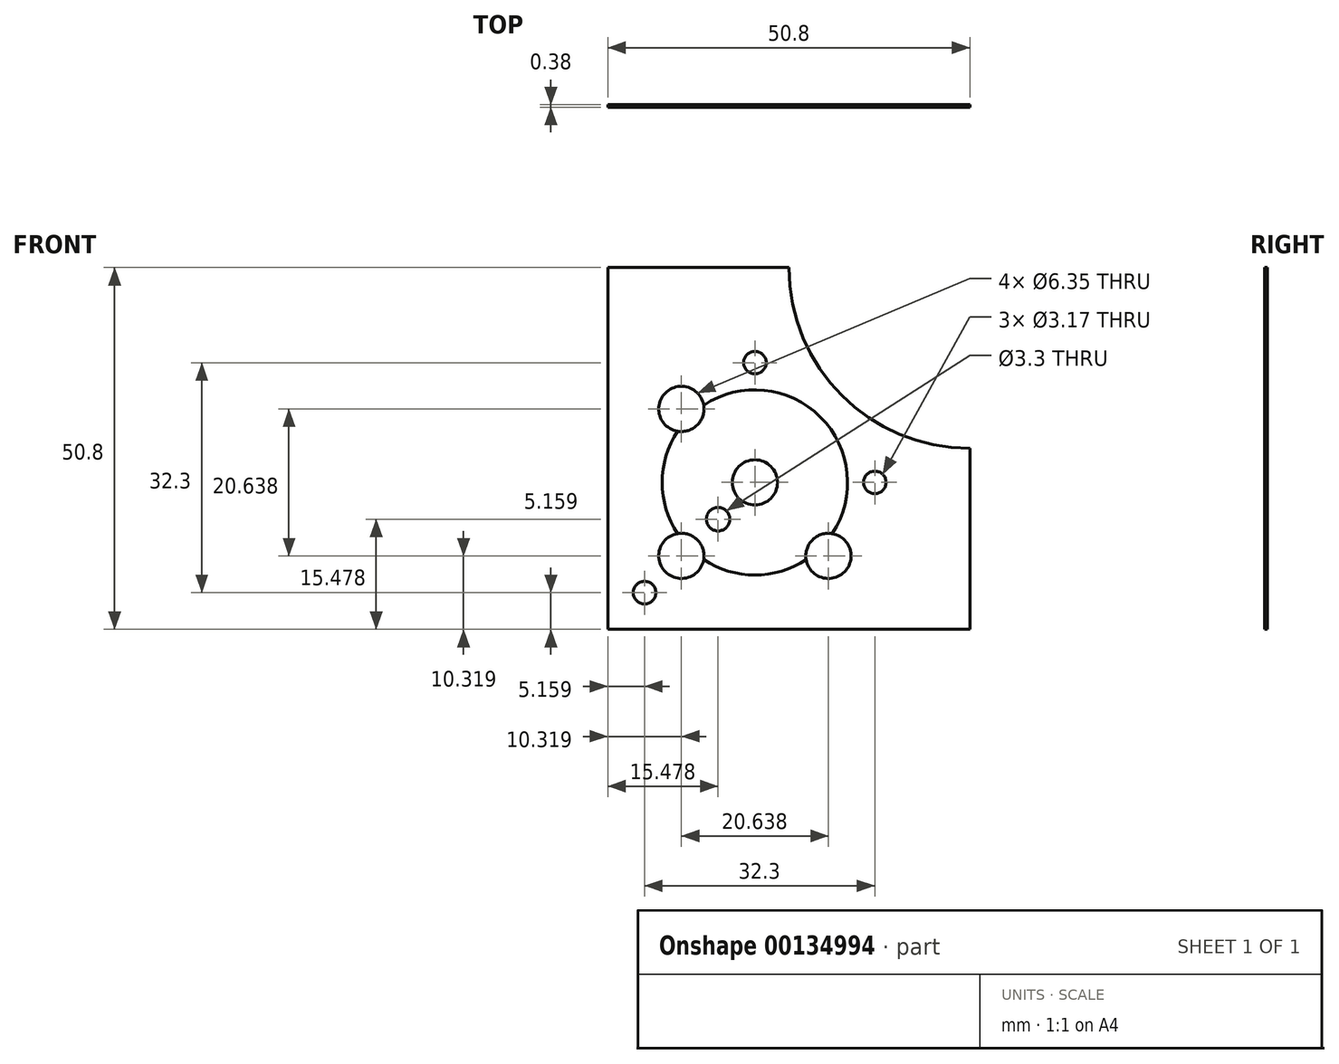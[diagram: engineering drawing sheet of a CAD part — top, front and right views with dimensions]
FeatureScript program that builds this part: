
annotation { "Feature Type Name" : "Feature", "Feature Type Description" : "" }
export const myFeature = defineFeature(function(context is Context, id is Id, definition is map)
    precondition{}
    {
        {
            assignVariable(context, id + "F0", {"name" : "Thickness", "anyValue" : .375});
        }
        {
            var Q0;
            Q0=qCreatedBy(makeId("Front.planeOp"),FACE);
            var sketch = newSketch(context, id + "F1", { "sketchPlane" : qUnion([Q0])});
            skLineSegment(sketch, "E0.bottom", {"start": v(0, 0) * mm, "end": v(50.8, 0) * mm});
            skLineSegment(sketch, "E0.top", {"start": v(0, 50.8) * mm, "end": v(25.4, 50.8) * mm});
            skLineSegment(sketch, "E0.left", {"start": v(0, 0) * mm, "end": v(0, 50.8) * mm});
            skLineSegment(sketch, "E0.right", {"start": v(50.8, 0) * mm, "end": v(50.8, 25.4) * mm});
            skPoint(sketch, "E1.orphan", {"position": v(50.8, 50.8) * mm});
            skArc(sketch, "E2", {"start": v(25.4, 50.8) * mm, "mid": v(32.84, 32.84) * mm, "end": v(50.8, 25.4) * mm});
            skSolve(sketch);
        }
        {
            var Q0;
            Q0=qCreatedBy(makeId("Front.planeOp"),FACE);
            var sketch = newSketch(context, id + "F2", { "sketchPlane" : qUnion([Q0])});
            skCircle(sketch, "E3", {"center": v(10.32, 10.32) * mm, "radius": 3.18 * mm});
            skCircle(sketch, "E4.0.1.0", {"center": v(10.32, 30.96) * mm, "radius": 3.18 * mm});
            skCircle(sketch, "E4.1.0.0", {"center": v(30.96, 10.32) * mm, "radius": 3.18 * mm});
            skLineSegment(sketch, "E4.direction1", {"start": v(10.32, 10.32) * mm, "end": v(30.96, 10.32) * mm, "construction": true});
            skLineSegment(sketch, "E4.direction2", {"start": v(10.32, 10.32) * mm, "end": v(10.32, 30.96) * mm, "construction": true});
            skSolve(sketch);
        }
        {
            var Q0;
            Q0=qCreatedBy(makeId("Front.planeOp"),FACE);
            var sketch = newSketch(context, id + "F3", { "sketchPlane" : qUnion([Q0])});
            skCircle(sketch, "E5", {"center": v(20.64, 20.64) * mm, "radius": 13 * mm});
            skSolve(sketch);
        }
        {
            var Q0;
            Q0=qCreatedBy(makeId("Front.planeOp"),FACE);
            var sketch = newSketch(context, id + "F4", { "sketchPlane" : qUnion([Q0])});
            skCircle(sketch, "E6", {"center": v(20.64, 3.82) * mm, "radius": 1.59 * mm, "construction": true});
            skLineSegment(sketch, "E7", {"start": v(20.64, 0) * mm, "end": v(20.64, 7.63) * mm, "construction": true});
            skLineSegment(sketch, "E8", {"start": v(0, 0) * mm, "end": v(10.32, 10.32) * mm, "construction": true});
            skLineSegment(sketch, "E9", {"start": v(10.32, 30.96) * mm, "end": v(30.96, 10.32) * mm, "construction": true});
            skCircle(sketch, "E10.MirrorC", {"center": v(37.46, 20.64) * mm, "radius": 1.59 * mm});
            skCircle(sketch, "E11.MirrorC", {"center": v(3.82, 20.64) * mm, "radius": 1.59 * mm, "construction": true});
            skCircle(sketch, "E12.MirrorC", {"center": v(20.64, 37.46) * mm, "radius": 1.59 * mm});
            skCircle(sketch, "E13", {"center": v(5.16, 5.16) * mm, "radius": 1.59 * mm});
            skSolve(sketch);
        }
        {
            var Q0;
            Q0=qCreatedBy(makeId("Front.planeOp"),FACE);
            var sketch = newSketch(context, id + "F5", { "sketchPlane" : qUnion([Q0])});
            skCircle(sketch, "E14", {"center": v(15.48, 15.48) * mm, "radius": 1.65 * mm});
            skLineSegment(sketch, "E15", {"start": v(10.32, 10.32) * mm, "end": v(20.64, 20.64) * mm, "construction": true});
            skSolve(sketch);
        }
        {
            var Q0;
            Q0=qCreatedBy(makeId("Front.planeOp"),FACE);
            var sketch = newSketch(context, id + "F6", { "sketchPlane" : qUnion([Q0])});
            skCircle(sketch, "E16", {"center": v(20.64, 20.64) * mm, "radius": 3.18 * mm});
            skSolve(sketch);
        }
        {
            var Q0;
            Q0=makeQuery(id+"F1.imprint","IMPRINT",FACE,{"disambiguationData":[TD([[makeQuery(id+"F1.imprint","IMPRINT",EDGE,{"derivedFrom":sQuery(id+"F1.wireOp",EDGE,"E0.bottom")}),1.0]])]});
            extrude(context, id + "F7", {"entities" : qUnion([Q0]), "depth" : (getVariable(context, 'Thickness') * 2 / 3) * mm, "hasSecondDirection" : true, "secondDirectionOppositeDirection" : true, "secondDirectionDepth" : (getVariable(context, 'Thickness') / 3) * mm});
        }
        {
            var Q0;
            Q0 = qSketchRegion(id + "F2", true);
            var Q1;
            Q1 = qSketchRegion(id + "F3", true);
            var Q2;
            Q2 = qSketchRegion(id + "F4", true);
            extrude(context, id + "F8", {"entities" : qUnion([Q0, Q1, Q2]), "operationType" : NewBodyOperationType.REMOVE, "depth" : 25.4 * mm});
        }
        {
            var Q0;
            Q0 = qSketchRegion(id + "F4", true);
            var Q1;
            Q1 = qSketchRegion(id + "F5", true);
            var Q2;
            Q2 = qSketchRegion(id + "F6", true);
            var Q3;
            Q3 = qSketchRegion(id + "F2", true);
            extrude(context, id + "F9", {"entities" : qUnion([Q0, Q1, Q2, Q3]), "operationType" : NewBodyOperationType.REMOVE, "endBound" : BoundingType.THROUGH_ALL, "oppositeDirection" : true, "depth" : 25.4 * mm});
        }
    });
